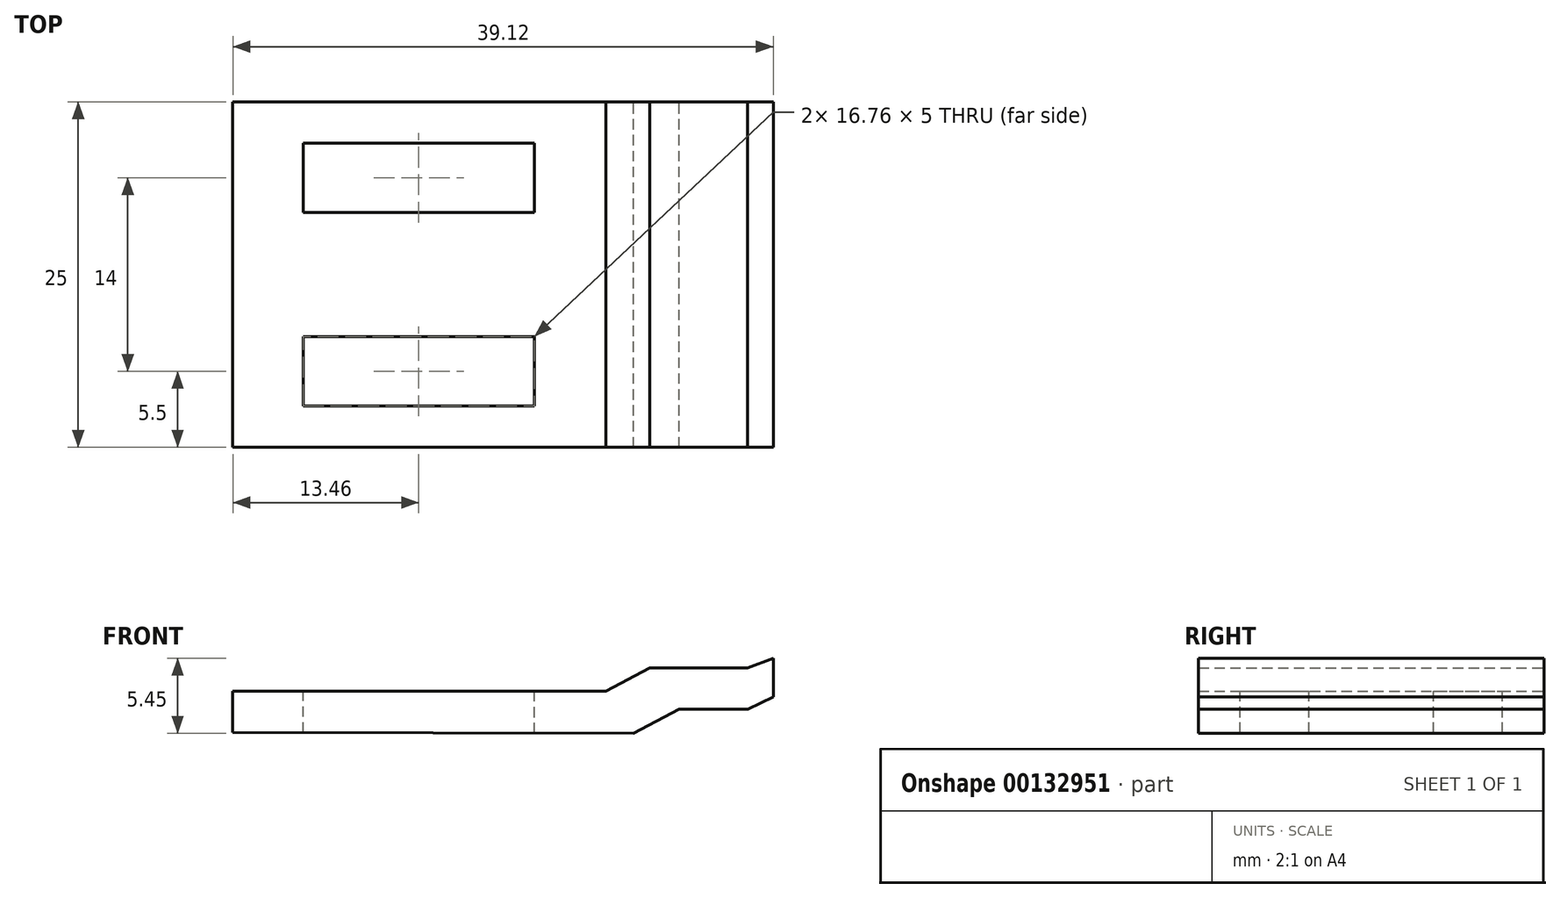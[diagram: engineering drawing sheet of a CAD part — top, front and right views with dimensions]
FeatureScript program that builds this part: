
annotation { "Feature Type Name" : "Feature", "Feature Type Description" : "" }
export const myFeature = defineFeature(function(context is Context, id is Id, definition is map)
    precondition{}
    {
        {
            var Q0;
            Q0=qCreatedBy(makeId("Front.planeOp"),FACE);
            var sketch = newSketch(context, id + "F0", { "sketchPlane" : qUnion([Q0])});
            skLineSegment(sketch, "E0", {"start": v(-5.08, 3.06) * mm, "end": v(21.92, 3.06) * mm});
            skLineSegment(sketch, "E1", {"start": v(21.92, 3.06) * mm, "end": v(25.1, 4.75) * mm});
            skLineSegment(sketch, "E2", {"start": v(25.1, 4.75) * mm, "end": v(32.16, 4.75) * mm});
            skLineSegment(sketch, "E3", {"start": v(32.16, 4.75) * mm, "end": v(34.04, 5.45) * mm});
            skLineSegment(sketch, "E4", {"start": v(34.04, 5.45) * mm, "end": v(34.04, 2.63) * mm});
            skLineSegment(sketch, "E5", {"start": v(34.04, 2.63) * mm, "end": v(32.2, 1.75) * mm});
            skLineSegment(sketch, "E6", {"start": v(32.2, 1.75) * mm, "end": v(27.2, 1.75) * mm});
            skLineSegment(sketch, "E7", {"start": v(27.2, 1.75) * mm, "end": v(23.92, 0) * mm});
            skLineSegment(sketch, "E8", {"start": v(23.92, 0) * mm, "end": v(-5.08, 0.06) * mm});
            skLineSegment(sketch, "E9", {"start": v(-5.08, 0.06) * mm, "end": v(-5.08, 3.06) * mm});
            skSolve(sketch);
        }
        {
            var Q0;
            Q0=makeQuery(id+"F0.imprint","IMPRINT",FACE,{"disambiguationData":[TD([[makeQuery(id+"F0.imprint","IMPRINT",EDGE,{"derivedFrom":sQuery(id+"F0.wireOp",EDGE,"E0")}),-1.0]])]});
            extrude(context, id + "F1", {"entities" : qUnion([Q0]), "depth" : 25 * mm});
        }
        {
            var Q0;
            Q0=makeQuery(id+"F1.opExtrude","SWEPT_FACE",FACE,{"disambiguationData":[OSD([sQuery(id+"F0.wireOp",EDGE,"E0")])]});
            var sketch = newSketch(context, id + "F2", { "sketchPlane" : qUnion([Q0])});
            skLineSegment(sketch, "E10.bottom", {"start": v(0, -22) * mm, "end": v(16.76, -22) * mm});
            skLineSegment(sketch, "E10.top", {"start": v(0, -17) * mm, "end": v(16.76, -17) * mm});
            skLineSegment(sketch, "E10.left", {"start": v(0, -22) * mm, "end": v(0, -17) * mm});
            skLineSegment(sketch, "E10.right", {"start": v(16.76, -22) * mm, "end": v(16.76, -17) * mm});
            skLineSegment(sketch, "E11.bottom", {"start": v(0, -8) * mm, "end": v(16.76, -8) * mm});
            skLineSegment(sketch, "E11.top", {"start": v(0, -3) * mm, "end": v(16.76, -3) * mm});
            skLineSegment(sketch, "E11.left", {"start": v(0, -8) * mm, "end": v(0, -3) * mm});
            skLineSegment(sketch, "E11.right", {"start": v(16.76, -8) * mm, "end": v(16.76, -3) * mm});
            skSolve(sketch);
        }
        {
            var Q0;
            Q0=makeQuery(id+"F2.imprint","IMPRINT",FACE,{"disambiguationData":[TD([[makeQuery(id+"F2.imprint","IMPRINT",EDGE,{"derivedFrom":sQuery(id+"F2.wireOp",EDGE,"E11.bottom")}),1.0]])]});
            var Q1;
            Q1=makeQuery(id+"F2.imprint","IMPRINT",FACE,{"disambiguationData":[TD([[makeQuery(id+"F2.imprint","IMPRINT",EDGE,{"derivedFrom":sQuery(id+"F2.wireOp",EDGE,"E10.bottom")}),1.0]])]});
            extrude(context, id + "F3", {"entities" : qUnion([Q0, Q1]), "operationType" : NewBodyOperationType.REMOVE, "oppositeDirection" : true, "depth" : 25 * mm});
        }
    });
